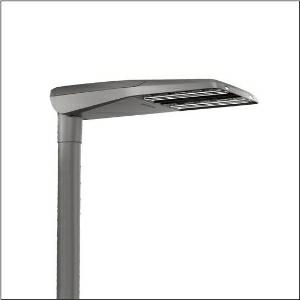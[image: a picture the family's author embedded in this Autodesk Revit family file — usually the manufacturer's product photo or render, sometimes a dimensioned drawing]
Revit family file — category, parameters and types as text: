
# Revit family: streetlight_sl_11_iq_midi___st1_2a_5xc3a51f08me_8c89
name_source: partatom
category: Lighting Fixtures
units: mm (PartAtom-declared; Revit-internal decimal feet)

## family parameters
Cut with Voids When Loaded = No
Host = Face
Light Source = No
Part Type = Normal
Room Calculation Point = No
Round Connector Dimension = Use Diameter
Shared = No

## types (1)
- --- (1 x LED, 18110 lm, 124.7 W, 3000K)
    Apparent Load = 125 VA
    CIE Flux Codes = 32 70 96 100 100
    Color Rendering = 70
    Color Temperature = 3000K
    Default Elevation = 1800 mm
    Description = Streetlight SL 11 iQ midi, mast luminaire, primary light control with 3 zone facetted reflector, of plastic, silver coated, highly specular, primary optical cover: cover, of PMMA, transparent, light distribution: ST1.2a, light emission: direct distribution, primary light characteristic: asymmetric, installation type: post-top, side-entry, lamps: LED, High Power LED, rated values: 18.110lm | 124,7W | 145,2lm/W (begin service life); end service life: 18.110lm | 132,2W; at 50% lumin. flux: 9.055lm | 57,2W | 158,3lm/W, colour temperature: 3000K, colour rendering: CRI > 70, light colour: 730, light setting 1 begin service life: 100% | 18.110lm | 124,7W | 145,2lm/W | 3.000K, light setting 1 end service life: 132,2W, further light settings possible, control: Street-Remote, optimised constant luminous flux control (CLO 2.0), Desk-Remote (wireless, voltage-free reading and setting of iQ features in the workshop via application-optimized NFC function/RFID function), Light-Fading, Smart-Wire, Night-Set, Lumen-Switch, Temp-Guard, Auto-Match, with cable H07RN-F 5x 1.5mm², mains connection: 230..240V, AC, 50/60Hz, connection cable pre-assembled, cable length: 12,5m, luminaire housing, of diecast aluminium, powder-coated, Siteco® metallic grey (DB 702S), please order mast flange separately, inclination adjustable without tools: 0°, 5°, 10°, 15° (post-top) | 0°, -5°, -10°, -15° (side-entry), sealing non-destructively replaceable, multi-level sealing system, length: 780mm, width: 376mm, height: 118mm, mast flange for spigot size: 42mm (side-entry): 5XC10008XM4, 60/48mm (side-entry/post-top): 5XC10108XM2, 76/60mm (side-entry/post-top): 5XC10108XM1, equipment: Power, protection rating (complete): IP66, insulation class (complete): insulation class II (safety insulation), certification: CE, ENEC, ENEC+, VDE, impact resistance: IK10, permissible operating ambient temperature for outdoor applications: -25..+50°C, standard-compliant lighting for roads and squares, Environmental Product Declaration (EPD) tested and certified by an independent institute, packaging unit: 1 piece

Light Distribution: ST1.2a
    Height = 118 mm
    Lamp = 1 x LED
    Lamp Light Flux = 18110 lm
    Lamp Power = 124.7 W
    Lamp count = 1
    Length = 780 mm
    Luminous efficacy = 145 lm/W
    Manufacturer = Siteco
    ModVariant = No
    Model = 5XC3A51F08ME
    Number of Poles = 1
    OnlyDefault = Yes
    Power Factor = 1
    Product Name = Streetlight SL 11 iQ midi | ST1.2a
    Product group = mast luminaire | pylon top
    ProductGroupID = 6100
    Protection Class = Protection class II
    Protection Degree = IP 66
    RLX_Detail_Level = 1
    RLX_Emergency_Light_Flux = 0 lm
    RLX_Emergency_Type = 0
    RLX_Emergency_Type_DB = No
    RlxData = <blob elided: 71161 chars, md5=573daf7d>
    Socket = socket
    Standby Power = 0 W
    System Light Flux = 18110 lm
    System Power = 125 W
    Type Comments = factory setting: luminous flux: 100 % | dim-lin: 254 | 557 mA
    Type Image = l_1005960.jpg
    URL = http://relux.com
    VarID = @adj_217521
    Voltage = 0 V
    Weight = 0.00 kg
    Width = 376 mm

## geometry (parser evidence)
native form markers: Blend x4, Sweep x8
no freeform markers — native parametric forms only
